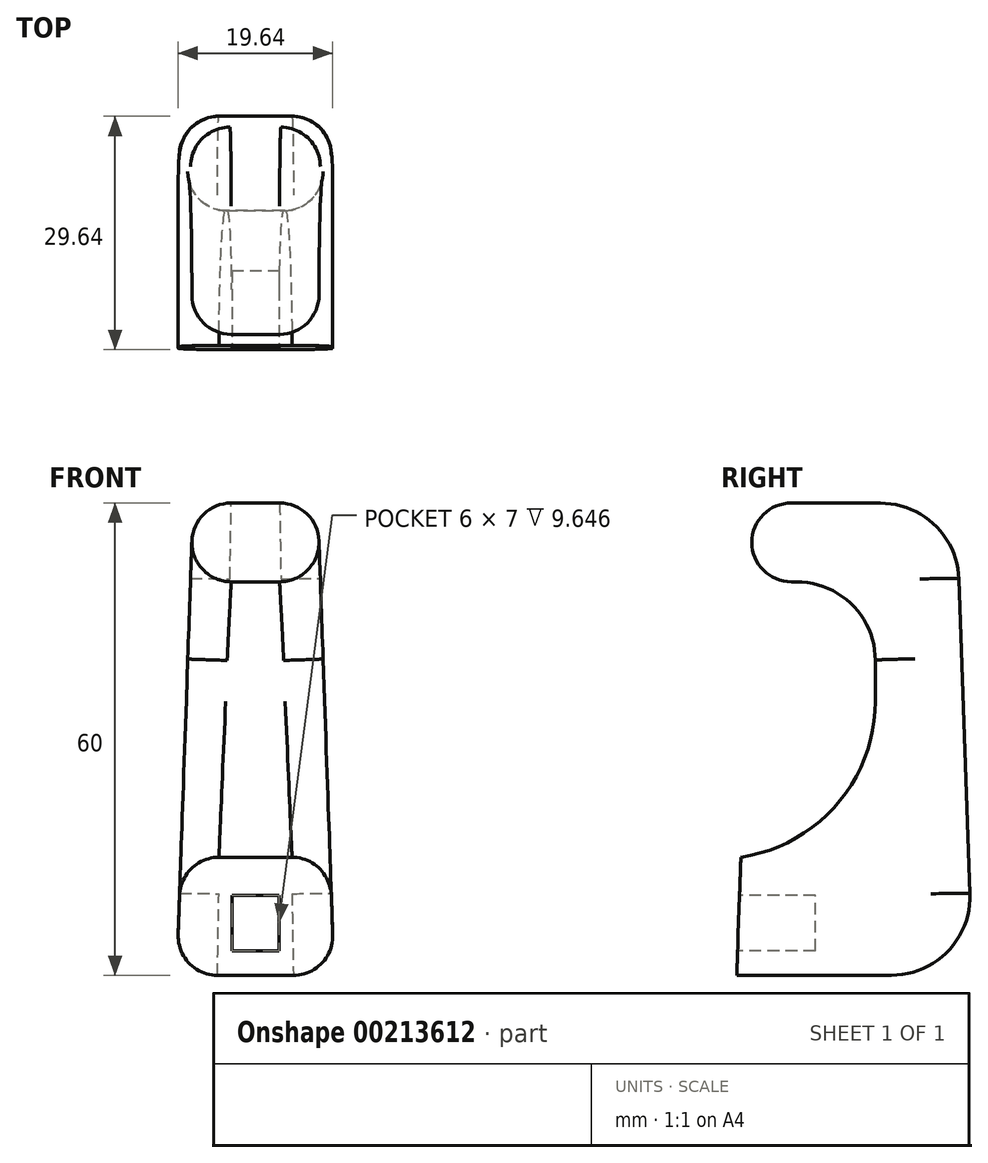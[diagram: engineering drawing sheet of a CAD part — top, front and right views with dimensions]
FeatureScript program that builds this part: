
annotation { "Feature Type Name" : "Feature", "Feature Type Description" : "" }
export const myFeature = defineFeature(function(context is Context, id is Id, definition is map)
    precondition{}
    {
        {
            var Q0;
            Q0=qCreatedBy(makeId("Top.planeOp"),FACE);
            var sketch = newSketch(context, id + "F0", { "sketchPlane" : qUnion([Q0])});
            skLineSegment(sketch, "E0.bottom", {"start": v(-10, -15) * mm, "end": v(10, -15) * mm});
            skLineSegment(sketch, "E0.top", {"start": v(-10, 15) * mm, "end": v(10, 15) * mm});
            skLineSegment(sketch, "E0.left", {"start": v(-10, -15) * mm, "end": v(-10, 15) * mm});
            skLineSegment(sketch, "E0.right", {"start": v(10, -15) * mm, "end": v(10, 15) * mm});
            skPoint(sketch, "E0.middle", {"position": v(0, 0) * mm});
            skSolve(sketch);
        }
        {
            var Q0;
            Q0=qSketchRegion(id+"F0",true);
            extrude(context, id + "F1", {"entities" : qUnion([Q0]), "depth" : 60 * mm, "hasDraft" : true, "draftAngle" : 2 * degree, "draftPullDirection" : true});
        }
        {
            var Q0;
            Q0=qCreatedBy(makeId("Right.planeOp"),FACE);
            var Q1;
            Q1=makeQuery(id+"F1.opExtrude","CAP_EDGE",EDGE,{"disambiguationData":[OSD([sQuery(id+"F0.wireOp",EDGE,"E0.left")])],"isStart":true});
            cPlane(context, id + "F2", {"entities" : qUnion([Q0, Q1]), "cplaneType" : CPlaneType.LINE_ANGLE, "offset" : 25 * mm, "angle" : 0 * degree, "width" : 150 * mm, "height" : 150 * mm});
        }
        {
            var Q0;
            Q0=qCreatedBy(id+"F2.planeOp",FACE);
            var sketch = newSketch(context, id + "F3", { "sketchPlane" : qUnion([Q0])});
            skLineSegment(sketch, "E1.bottom", {"start": v(12.38, 45) * mm, "end": v(-2.62, 45) * mm});
            skLineSegment(sketch, "E1.top", {"start": v(12.38, 15) * mm, "end": v(-2.62, 15) * mm});
            skLineSegment(sketch, "E1.right", {"start": v(-2.62, 45) * mm, "end": v(-2.62, 15) * mm});
            skLineSegment(sketch, "E2", {"start": v(12.38, 15) * mm, "end": v(14.48, 15) * mm});
            skLineSegment(sketch, "E3", {"start": v(13.95, 30) * mm, "end": v(14.48, 15) * mm});
            skLineSegment(sketch, "E4", {"start": v(12.38, 45) * mm, "end": v(12.38, 15) * mm});
            skLineSegment(sketch, "E5", {"start": v(-2.62, 45) * mm, "end": v(-2.62, 50) * mm});
            skLineSegment(sketch, "E6", {"start": v(-2.62, 50) * mm, "end": v(13.25, 50) * mm});
            skLineSegment(sketch, "E7", {"start": v(13.25, 50) * mm, "end": v(13.95, 30) * mm});
            skSolve(sketch);
        }
        {
            var Q0;
            Q0=qSketchRegion(id+"F3",true);
            extrude(context, id + "F4", {"entities" : qUnion([Q0]), "operationType" : NewBodyOperationType.REMOVE, "endBound" : BoundingType.THROUGH_ALL, "oppositeDirection" : true, "depth" : 25 * mm});
        }
        {
            var Q0;
            Q0=makeQuery(id+"F4.boolean.opBoolean","COPY",EDGE,{"derivedFrom":makeQuery(id+"F4.opExtrude","SWEPT_EDGE",EDGE,{"disambiguationData":[OSD([sQuery(id+"F3.wireOp",EDGE,"E1.top"),sQuery(id+"F3.wireOp",EDGE,"E1.right")])]})});
            fillet(context, id + "F5", {"entities" : qUnion([Q0]), "radius" : 20 * mm, "tangentPropagation" : true, "allowEdgeOverflow" : false});
        }
        {
            var Q0;
            Q0=qCreatedBy(makeId("Front.planeOp"),FACE);
            var Q1;
            Q1=makeQuery(id+"F1.opExtrude","CAP_EDGE",EDGE,{"disambiguationData":[OSD([sQuery(id+"F0.wireOp",EDGE,"E0.bottom")])],"isStart":true});
            cPlane(context, id + "F6", {"entities" : qUnion([Q0, Q1]), "cplaneType" : CPlaneType.LINE_ANGLE, "offset" : 25 * mm, "angle" : 0 * degree, "width" : 150 * mm, "height" : 150 * mm});
        }
        {
            var Q0;
            Q0=qCreatedBy(id+"F6.planeOp",FACE);
            var sketch = newSketch(context, id + "F7", { "sketchPlane" : qUnion([Q0])});
            skLineSegment(sketch, "E8.bottom", {"start": v(3, 3.13) * mm, "end": v(-3, 3.13) * mm});
            skLineSegment(sketch, "E8.top", {"start": v(3, 10.13) * mm, "end": v(-3, 10.13) * mm});
            skLineSegment(sketch, "E8.left", {"start": v(3, 3.13) * mm, "end": v(3, 10.13) * mm});
            skLineSegment(sketch, "E8.right", {"start": v(-3, 3.13) * mm, "end": v(-3, 10.13) * mm});
            skPoint(sketch, "E8.middle", {"position": v(0, 6.63) * mm});
            skSolve(sketch);
        }
        {
            var Q0;
            Q0=qSketchRegion(id+"F7",true);
            extrude(context, id + "F8", {"entities" : qUnion([Q0]), "operationType" : NewBodyOperationType.REMOVE, "depth" : 10 * mm});
        }
        {
            var Q0;
            Q0=makeQuery(id+"F1.opExtrude","CAP_EDGE",EDGE,{"disambiguationData":[OSD([sQuery(id+"F0.wireOp",EDGE,"E0.top")])],"isStart":true});
            fillet(context, id + "F9", {"entities" : qUnion([Q0]), "radius" : 10 * mm, "tangentPropagation" : true, "allowEdgeOverflow" : false});
        }
        {
            var Q0;
            Q0=makeQuery(id+"F4.boolean.opBoolean","COPY",EDGE,{"derivedFrom":makeQuery(id+"F4.opExtrude","SWEPT_EDGE",EDGE,{"disambiguationData":[OSD([sQuery(id+"F3.wireOp",EDGE,"E5"),sQuery(id+"F3.wireOp",EDGE,"E6")])]})});
            var Q1;
            Q1=makeQuery(id+"F1.opExtrude","CAP_EDGE",EDGE,{"disambiguationData":[OSD([sQuery(id+"F0.wireOp",EDGE,"E0.top")])],"isStart":false});
            fillet(context, id + "F10", {"entities" : qUnion([Q0, Q1]), "radius" : 10 * mm, "tangentPropagation" : true, "allowEdgeOverflow" : false});
        }
        {
            var Q0;
            Q0=makeQuery(id+"F1.opExtrude","CAP_EDGE",EDGE,{"disambiguationData":[OSD([sQuery(id+"F0.wireOp",EDGE,"E0.bottom")])],"isStart":false});
            var Q1;
            Q1=makeQuery(id+"F4.boolean.opBoolean","COPY",EDGE,{"derivedFrom":makeQuery(id+"F4.opExtrude","SWEPT_EDGE",EDGE,{"disambiguationData":[OSD([sQuery(id+"F3.wireOp",EDGE,"E6"),sQuery(id+"F3.wireOp",EDGE,"E7")])]})});
            fillet(context, id + "F11", {"entities" : qUnion([Q0, Q1]), "radius" : 5 * mm, "tangentPropagation" : true, "allowEdgeOverflow" : false});
        }
        {
            var Q0;
            Q0=makeQuery(id+"F5.opFillet","BLEND_EDGE",EDGE,{"blendedFrom":[makeQuery(id+"F4.boolean.opBoolean","COPY",EDGE,{"derivedFrom":makeQuery(id+"F4.opExtrude","SWEPT_EDGE",EDGE,{"disambiguationData":[OSD([sQuery(id+"F3.wireOp",EDGE,"E1.top"),sQuery(id+"F3.wireOp",EDGE,"E1.right")])]})}),makeQuery(id+"F1.opExtrude","SWEPT_FACE",FACE,{"disambiguationData":[OSD([sQuery(id+"F0.wireOp",EDGE,"E0.left")])]})],"blendedInto":[makeQuery(id+"F1.opExtrude","SWEPT_FACE",FACE,{"disambiguationData":[OSD([sQuery(id+"F0.wireOp",EDGE,"E0.left")])]})]});
            var Q1;
            Q1=makeQuery(id+"F5.opFillet","BLEND_EDGE",EDGE,{"blendedFrom":[makeQuery(id+"F4.boolean.opBoolean","COPY",EDGE,{"derivedFrom":makeQuery(id+"F4.opExtrude","SWEPT_EDGE",EDGE,{"disambiguationData":[OSD([sQuery(id+"F3.wireOp",EDGE,"E1.top"),sQuery(id+"F3.wireOp",EDGE,"E1.right")])]})}),makeQuery(id+"F1.opExtrude","SWEPT_FACE",FACE,{"disambiguationData":[OSD([sQuery(id+"F0.wireOp",EDGE,"E0.right")])]})],"blendedInto":[makeQuery(id+"F1.opExtrude","SWEPT_FACE",FACE,{"disambiguationData":[OSD([sQuery(id+"F0.wireOp",EDGE,"E0.right")])]})]});
            fillet(context, id + "F12", {"entities" : qUnion([Q0, Q1]), "radius" : 5 * mm, "tangentPropagation" : true, "allowEdgeOverflow" : false});
        }
    });
